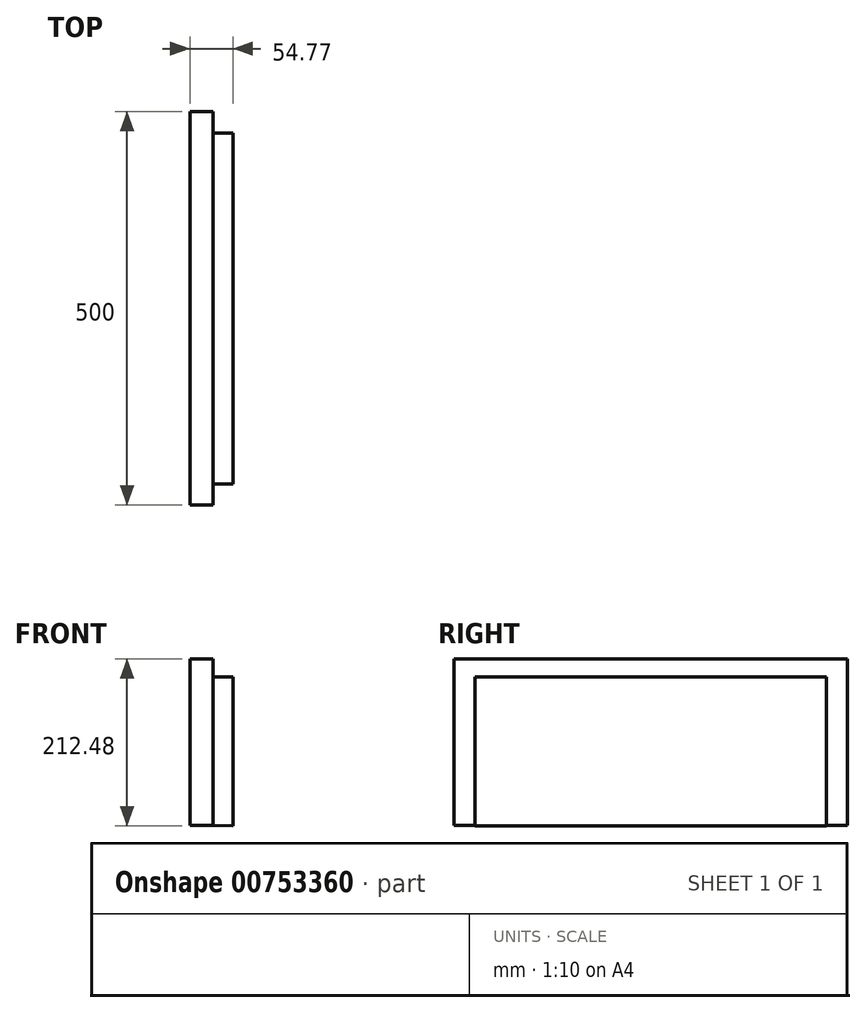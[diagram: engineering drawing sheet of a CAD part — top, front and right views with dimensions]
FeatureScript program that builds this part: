
annotation { "Feature Type Name" : "Feature", "Feature Type Description" : "" }
export const myFeature = defineFeature(function(context is Context, id is Id, definition is map)
    precondition{}
    {
        {
            var Q0;
            Q0=qCreatedBy(makeId("Front.planeOp"),FACE);
            var sketch = newSketch(context, id + "F0", { "sketchPlane" : qUnion([Q0])});
            skLineSegment(sketch, "E0", {"start": v(0, 0) * mm, "end": v(29.46, 0) * mm});
            skLineSegment(sketch, "E1", {"start": v(29.46, 0) * mm, "end": v(29.46, -23.44) * mm});
            skLineSegment(sketch, "E2", {"start": v(29.46, -23.44) * mm, "end": v(54.77, -23.44) * mm});
            skLineSegment(sketch, "E3", {"start": v(54.77, -23.44) * mm, "end": v(54.77, -64.93) * mm});
            skLineSegment(sketch, "E4", {"start": v(54.77, -64.93) * mm, "end": v(54.77, -212.48) * mm});
            skLineSegment(sketch, "E5", {"start": v(0, -211.5) * mm, "end": v(54.77, -212.48) * mm});
            skLineSegment(sketch, "E6", {"start": v(0, -211.5) * mm, "end": v(0, 0) * mm});
            skSolve(sketch);
        }
        {
            var Q0;
            Q0=makeQuery(id+"F0.imprint","IMPRINT",FACE,{"disambiguationData":[TD([[makeQuery(id+"F0.imprint","IMPRINT",EDGE,{"derivedFrom":sQuery(id+"F0.wireOp",EDGE,"E0")}),-1.0]])]});
            extrude(context, id + "F1", {"entities" : qUnion([Q0]), "depth" : 500 * mm, "offsetDistance" : 25.4 * mm});
        }
        {
            var Q0;
            Q0=makeQuery(id+"F1.opExtrude","SWEPT_FACE",FACE,{"disambiguationData":[OSD([sQuery(id+"F0.wireOp",EDGE,"E2")])]});
            var sketch = newSketch(context, id + "F2", { "sketchPlane" : qUnion([Q0])});
            skLineSegment(sketch, "E7.bottom", {"start": v(54.77, 0) * mm, "end": v(29.46, 0) * mm});
            skLineSegment(sketch, "E7.top", {"start": v(54.77, -27.04) * mm, "end": v(29.46, -27.04) * mm});
            skLineSegment(sketch, "E7.left", {"start": v(54.77, 0) * mm, "end": v(54.77, -27.04) * mm});
            skLineSegment(sketch, "E7.right", {"start": v(29.46, 0) * mm, "end": v(29.46, -27.04) * mm});
            skSolve(sketch);
        }
        {
            var Q0;
            Q0=makeQuery(id+"F2.imprint","IMPRINT",FACE,{"disambiguationData":[TD([[makeQuery(id+"F2.imprint","IMPRINT",EDGE,{"derivedFrom":sQuery(id+"F2.wireOp",EDGE,"E7.bottom")}),-1.0]])]});
            var Q1;
            Q1=makeQuery(id+"F1.opExtrude","SWEPT_FACE",FACE,{"disambiguationData":[OSD([sQuery(id+"F0.wireOp",EDGE,"E5")])]});
            extrude(context, id + "F3", {"entities" : qUnion([Q0, Q1]), "operationType" : NewBodyOperationType.REMOVE, "endBound" : BoundingType.THROUGH_ALL, "oppositeDirection" : true, "depth" : 25.4 * mm, "offsetDistance" : 25.4 * mm});
        }
        {
            var Q0;
            Q0=makeQuery(id+"F1.opExtrude","SWEPT_FACE",FACE,{"disambiguationData":[OSD([sQuery(id+"F0.wireOp",EDGE,"E2")])]});
            var sketch = newSketch(context, id + "F4", { "sketchPlane" : qUnion([Q0])});
            skLineSegment(sketch, "E8.bottom", {"start": v(54.77, -500) * mm, "end": v(29.46, -500) * mm});
            skLineSegment(sketch, "E8.top", {"start": v(54.77, -472.95) * mm, "end": v(29.46, -472.95) * mm});
            skLineSegment(sketch, "E8.left", {"start": v(54.77, -500) * mm, "end": v(54.77, -472.95) * mm});
            skLineSegment(sketch, "E8.right", {"start": v(29.46, -500) * mm, "end": v(29.46, -472.95) * mm});
            skSolve(sketch);
        }
        {
            var Q0;
            Q0=makeQuery(id+"F4.imprint","IMPRINT",FACE,{"disambiguationData":[TD([[makeQuery(id+"F4.imprint","IMPRINT",EDGE,{"derivedFrom":sQuery(id+"F4.wireOp",EDGE,"E8.bottom")}),1.0]])]});
            extrude(context, id + "F5", {"entities" : qUnion([Q0]), "operationType" : NewBodyOperationType.REMOVE, "endBound" : BoundingType.THROUGH_ALL, "oppositeDirection" : true, "depth" : 25.4 * mm, "offsetDistance" : 25.4 * mm});
        }
    });
